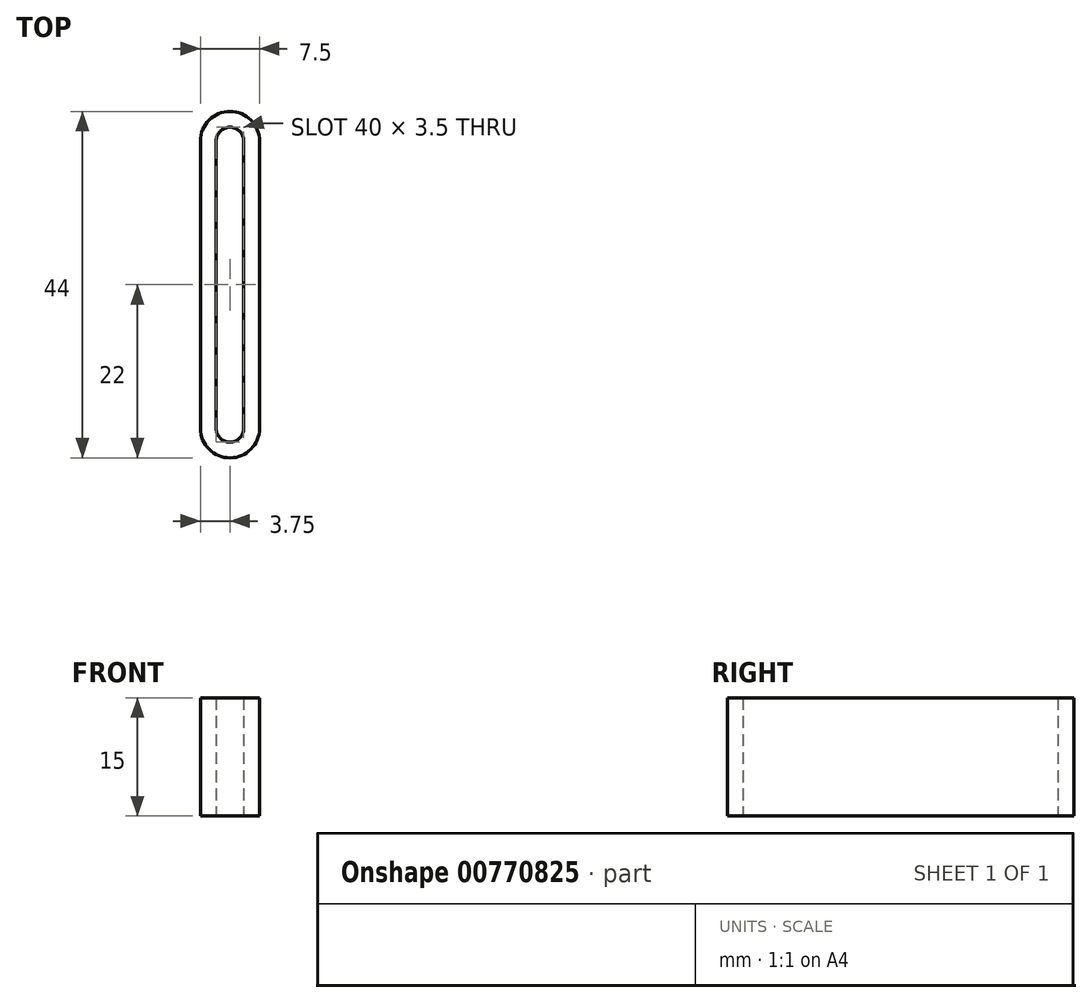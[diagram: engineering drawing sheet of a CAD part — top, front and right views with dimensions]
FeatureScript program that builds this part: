
annotation { "Feature Type Name" : "Feature", "Feature Type Description" : "" }
export const myFeature = defineFeature(function(context is Context, id is Id, definition is map)
    precondition{}
    {
        {
            var Q0;
            Q0=qCreatedBy(makeId("Top.planeOp"),FACE);
            var sketch = newSketch(context, id + "F0", { "sketchPlane" : qUnion([Q0])});
            skArc(sketch, "E0", {"start": v(1.75, 23.25) * mm, "mid": v(0, 25) * mm, "end": v(-1.75, 23.25) * mm});
            skArc(sketch, "E1", {"start": v(-1.75, -13.25) * mm, "mid": v(0, -15) * mm, "end": v(1.75, -13.25) * mm});
            skLineSegment(sketch, "E2", {"start": v(-1.75, 23.25) * mm, "end": v(-1.75, -13.25) * mm});
            skLineSegment(sketch, "E3", {"start": v(1.75, 23.25) * mm, "end": v(1.75, -13.25) * mm});
            skLineSegment(sketch, "E4.0", {"start": v(-3.75, 23.25) * mm, "end": v(-3.75, -13.25) * mm});
            skArc(sketch, "E4.1", {"start": v(3.75, 23.25) * mm, "mid": v(0, 27) * mm, "end": v(-3.75, 23.25) * mm});
            skLineSegment(sketch, "E4.2", {"start": v(3.75, 23.25) * mm, "end": v(3.75, -13.25) * mm});
            skArc(sketch, "E4.3", {"start": v(-3.75, -13.25) * mm, "mid": v(0, -17) * mm, "end": v(3.75, -13.25) * mm});
            skSolve(sketch);
        }
        {
            var Q0;
            Q0=makeQuery(id+"F0.imprint","IMPRINT",FACE,{"disambiguationData":[TD([[makeQuery(id+"F0.imprint","IMPRINT",EDGE,{"derivedFrom":sQuery(id+"F0.wireOp",EDGE,"E0")}),-1.0]])]});
            extrude(context, id + "F1", {"entities" : qUnion([Q0]), "depth" : 15 * mm, "offsetDistance" : 25 * mm});
        }
    });
